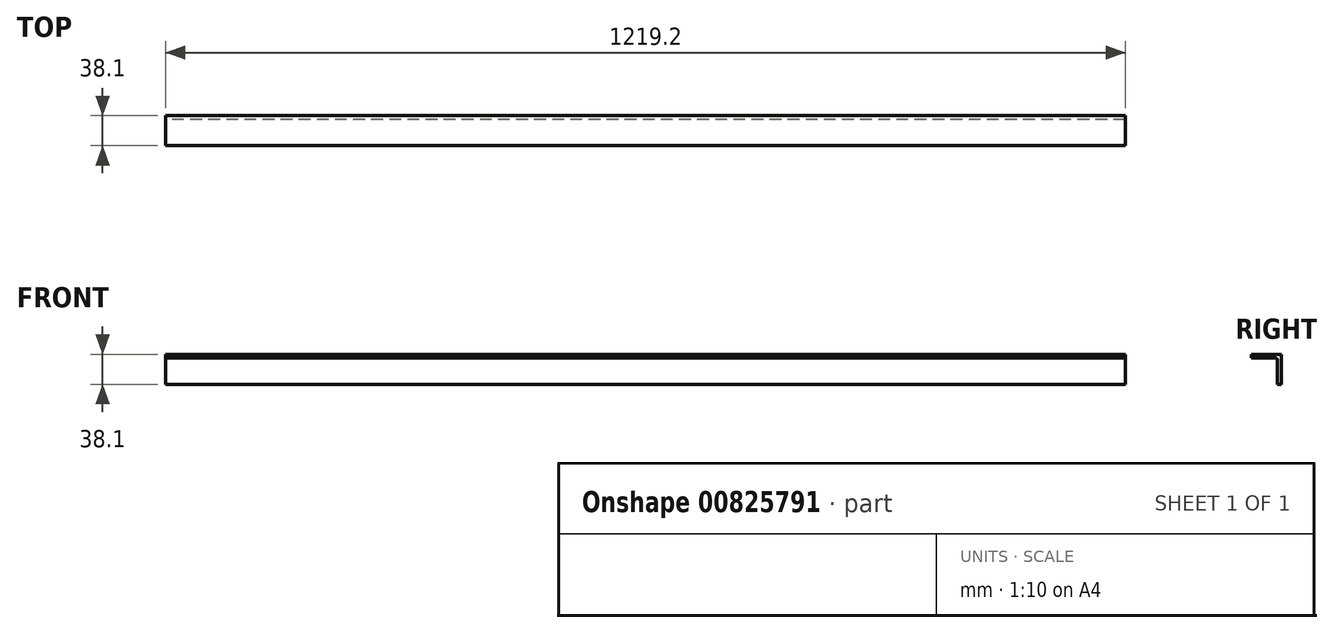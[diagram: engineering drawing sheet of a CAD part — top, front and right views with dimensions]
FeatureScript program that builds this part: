
annotation { "Feature Type Name" : "Feature", "Feature Type Description" : "" }
export const myFeature = defineFeature(function(context is Context, id is Id, definition is map)
    precondition{}
    {
        {
            var Q0;
            Q0=qCreatedBy(makeId("Right.planeOp"),FACE);
            var sketch = newSketch(context, id + "F0", { "sketchPlane" : qUnion([Q0])});
            skLineSegment(sketch, "E0", {"start": v(-3.18, 0) * mm, "end": v(-33.32, 0) * mm});
            skLineSegment(sketch, "E1", {"start": v(-33.32, 0) * mm, "end": v(-33.32, 4.78) * mm});
            skLineSegment(sketch, "E2", {"start": v(-33.32, 4.78) * mm, "end": v(4.78, 4.78) * mm});
            skLineSegment(sketch, "E3", {"start": v(4.78, 4.78) * mm, "end": v(4.78, -33.32) * mm});
            skLineSegment(sketch, "E4", {"start": v(4.78, -33.32) * mm, "end": v(0, -33.32) * mm});
            skLineSegment(sketch, "E5", {"start": v(0, -33.32) * mm, "end": v(0, -3.18) * mm});
            skPoint(sketch, "E6.visualSharp", {"position": v(0, 0) * mm});
            skArc(sketch, "E6.filletArc", {"start": v(0, -3.18) * mm, "mid": v(-0.93, -0.93) * mm, "end": v(-3.18, 0) * mm});
            skSolve(sketch);
        }
        {
            var Q0;
            Q0 = qSketchRegion(id + "F0", true);
            extrude(context, id + "F1", {"entities" : qUnion([Q0]), "depth" : 1219.2 * mm, "offsetDistance" : 25.4 * mm});
        }
    });
